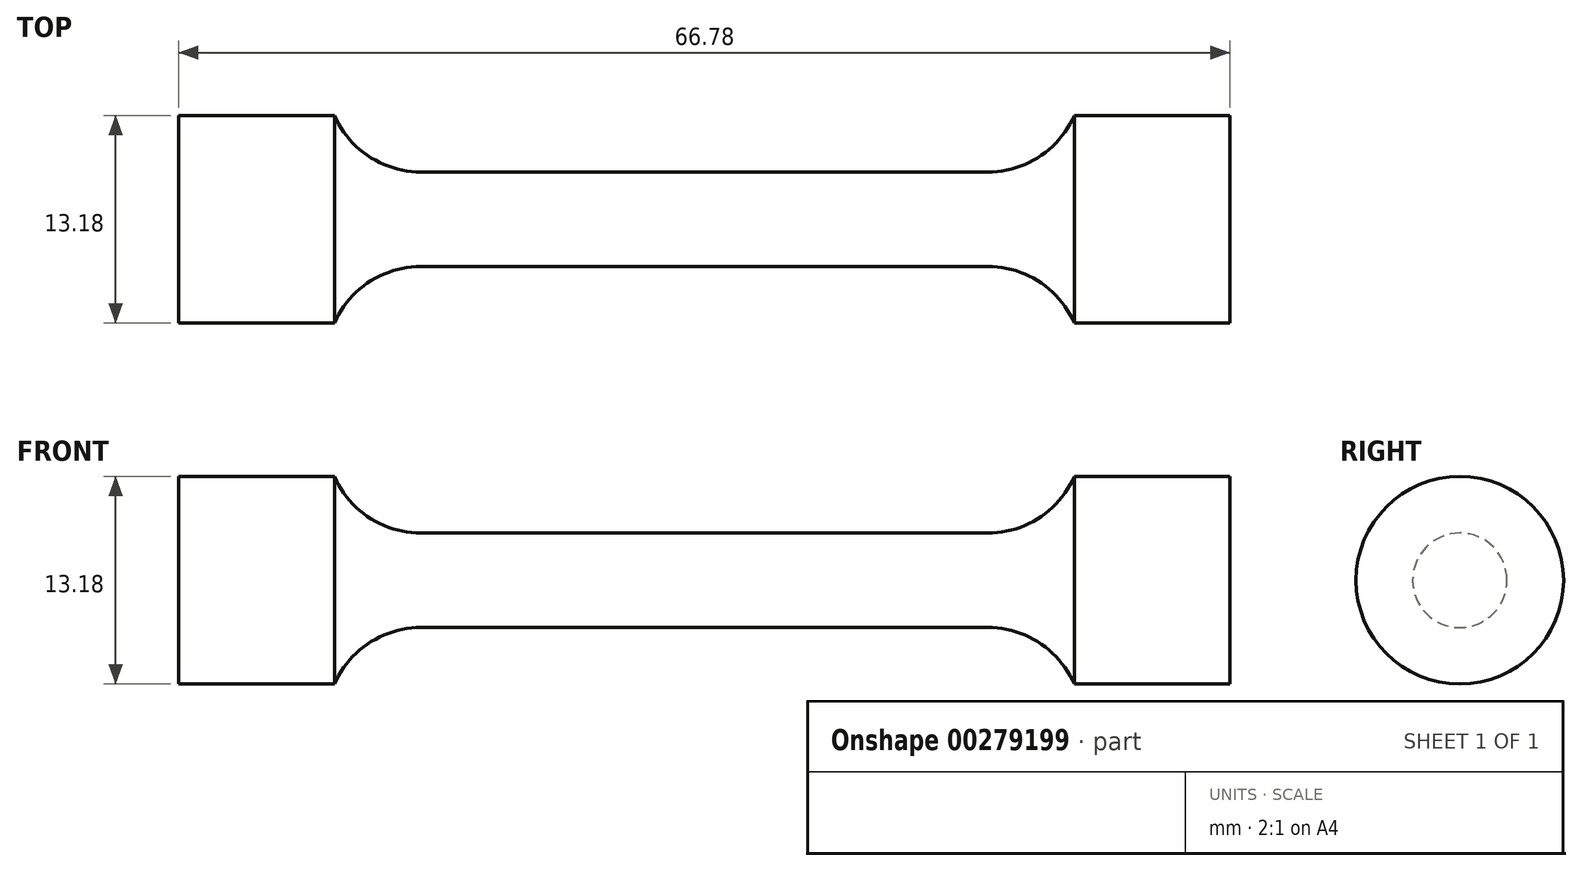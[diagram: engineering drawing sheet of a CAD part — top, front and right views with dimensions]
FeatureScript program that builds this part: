
annotation { "Feature Type Name" : "Feature", "Feature Type Description" : "" }
export const myFeature = defineFeature(function(context is Context, id is Id, definition is map)
    precondition{}
    {
        {
            var Q0;
            Q0=qCreatedBy(makeId("Front.planeOp"),FACE);
            var sketch = newSketch(context, id + "F0", { "sketchPlane" : qUnion([Q0])});
            skLineSegment(sketch, "E0", {"start": v(0, 3) * mm, "end": v(18, 3) * mm});
            skArc(sketch, "E1", {"start": v(18, 3) * mm, "mid": v(21.28, 3.98) * mm, "end": v(23.5, 6.6) * mm});
            skLineSegment(sketch, "E2", {"start": v(23.5, 6.6) * mm, "end": v(33.4, 6.6) * mm});
            skLineSegment(sketch, "E3", {"start": v(33.4, 6.6) * mm, "end": v(33.4, 0) * mm});
            skLineSegment(sketch, "E4.MirrorCS", {"start": v(0, 3) * mm, "end": v(-18, 3) * mm});
            skLineSegment(sketch, "E5.MirrorCS", {"start": v(-33.4, 6.6) * mm, "end": v(-33.4, 0) * mm});
            skLineSegment(sketch, "E6.MirrorCS", {"start": v(-23.5, 6.6) * mm, "end": v(-33.4, 6.6) * mm});
            skArc(sketch, "E7.MirrorCS", {"start": v(-18, 3) * mm, "mid": v(-21.28, 3.98) * mm, "end": v(-23.5, 6.6) * mm});
            skLineSegment(sketch, "E8", {"start": v(-33.4, 0) * mm, "end": v(33.4, 0) * mm});
            skSolve(sketch);
        }
        {
            var Q0;
            Q0=makeQuery(id+"F0.imprint","IMPRINT",FACE,{"disambiguationData":[TD([[makeQuery(id+"F0.imprint","IMPRINT",EDGE,{"derivedFrom":sQuery(id+"F0.wireOp",EDGE,"E0")}),-1.0]])]});
            var Q1;
            Q1=sQuery(id+"F0.wireOp",EDGE,"E8");
            revolve(context, id + "F1", {"entities" : qUnion([Q0]), "axis" : qUnion([Q1]), "revolveType" : RevolveType.FULL});
        }
    });
